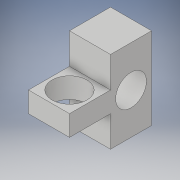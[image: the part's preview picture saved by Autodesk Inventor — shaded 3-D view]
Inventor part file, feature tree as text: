
AUTODESK INVENTOR PART (.ipt)
format: ipt  version: 2018 (Build 220112000, 112)  size: 130,560 bytes
history: native  units: mm
features: extrude x4, sketch x4
ambient origin geometry x8: Origin, YZ Plane, XZ Plane, XY Plane, X Axis, Y Axis, Z Axis, Center Point
bodies: Volumenkörper1 (feature_tree)
feature tree (8):
  extrude  "Extrusion1"  Depth=8.0mm
  extrude  "Extrusion10"  Depth=4.0mm
  extrude  "Extrusion11"  Depth=3.0mm
  extrude  "Extrusion12"  Depth=5.0mm TaperAngle=0.0deg
  sketch  "Skizze1"  dims[d0=4.0mm d1=8.0mm]
  sketch  "Skizze12"  dims[d2=8.0mm d3=0.0mm d45=4.0mm]
  sketch  "Skizze13"  dims[d46=4.0mm d47=3.0mm]
  sketch  "Skizze14"  dims[d48=3.0mm d49=5.0mm d50=0.0mm d51=3.4mm d52=2.0mm d53=2.0mm d54=3.0mm d55=0.0mm d56=3.0mm d57=4.0mm d58=2.0mm d59=10.0mm d60=0.0mm]
